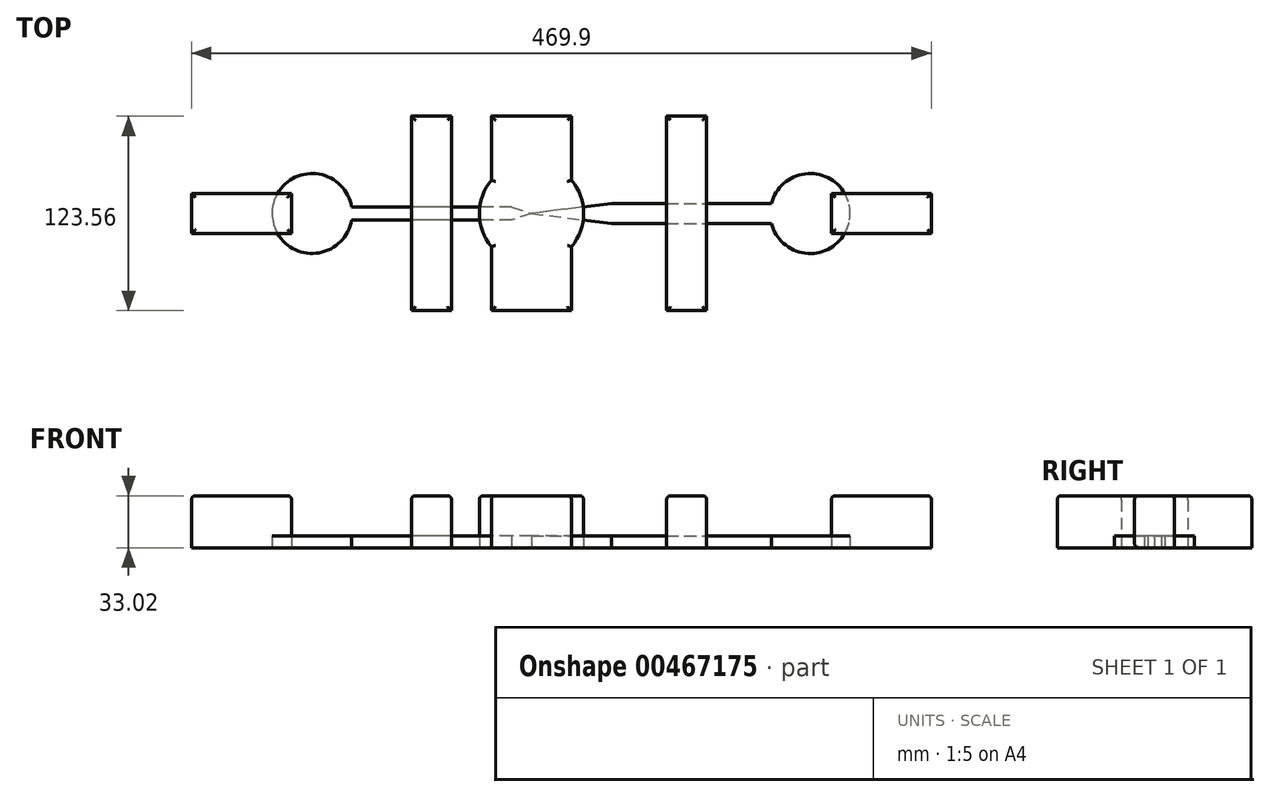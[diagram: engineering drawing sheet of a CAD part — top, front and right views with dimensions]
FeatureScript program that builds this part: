
annotation { "Feature Type Name" : "Feature", "Feature Type Description" : "" }
export const myFeature = defineFeature(function(context is Context, id is Id, definition is map)
    precondition{}
    {
        {
            var Q0;
            Q0=qCreatedBy(makeId("Top.planeOp"),FACE);
            var sketch = newSketch(context, id + "F0", { "sketchPlane" : qUnion([Q0])});
            skLineSegment(sketch, "E0.bottom", {"start": v(50.8, 4.22) * mm, "end": v(-50.8, 4.22) * mm});
            skLineSegment(sketch, "E0.top", {"start": v(50.8, -4.22) * mm, "end": v(-50.8, -4.22) * mm});
            skLineSegment(sketch, "E0.left", {"start": v(50.8, 4.22) * mm, "end": v(50.8, -4.22) * mm});
            skLineSegment(sketch, "E0.right", {"start": v(-50.8, 4.22) * mm, "end": v(-50.8, -4.22) * mm});
            skPoint(sketch, "E0.middle", {"position": v(0, 0) * mm});
            skLineSegment(sketch, "E1", {"start": v(50.8, 4.22) * mm, "end": v(63.5, 0) * mm});
            skLineSegment(sketch, "E2", {"start": v(63.5, 0) * mm, "end": v(50.8, -4.22) * mm});
            skCircle(sketch, "E3", {"center": v(-75.85, 0) * mm, "radius": 25.4 * mm});
            skPoint(sketch, "E3.third.point", {"position": v(-101.25, 0) * mm});
            skPoint(sketch, "E3.third.point.positionSnap0", {"position": v(-50.8, 0) * mm});
            skLineSegment(sketch, "E4.bottom", {"start": v(114.3, 6.45) * mm, "end": v(215.9, 6.45) * mm});
            skLineSegment(sketch, "E4.top", {"start": v(114.3, -6.45) * mm, "end": v(215.9, -6.45) * mm});
            skLineSegment(sketch, "E4.left", {"start": v(114.3, 6.45) * mm, "end": v(114.3, -6.45) * mm});
            skLineSegment(sketch, "E4.right", {"start": v(215.9, 6.45) * mm, "end": v(215.9, -6.45) * mm});
            skPoint(sketch, "E4.middle", {"position": v(165.1, 0) * mm});
            skLineSegment(sketch, "E5", {"start": v(114.3, 6.45) * mm, "end": v(63.5, 0) * mm});
            skLineSegment(sketch, "E6", {"start": v(63.5, 0) * mm, "end": v(114.3, -6.45) * mm});
            skCircle(sketch, "E7", {"center": v(240.47, 0) * mm, "radius": 25.4 * mm});
            skPoint(sketch, "E7.third.point", {"position": v(265.03, -6.45) * mm});
            skCircle(sketch, "E8", {"center": v(63.5, 0) * mm, "radius": 31.15 * mm});
            skLineSegment(sketch, "E9.bottom", {"start": v(-12.7, -76.2) * mm, "end": v(12.7, -76.2) * mm});
            skLineSegment(sketch, "E9.top", {"start": v(-12.7, 76.2) * mm, "end": v(12.7, 76.2) * mm});
            skLineSegment(sketch, "E9.left", {"start": v(-12.7, -76.2) * mm, "end": v(-12.7, 76.2) * mm});
            skLineSegment(sketch, "E9.right", {"start": v(12.7, -76.2) * mm, "end": v(12.7, 76.2) * mm});
            skLineSegment(sketch, "E10.bottom", {"start": v(152.4, 76.2) * mm, "end": v(177.8, 76.2) * mm});
            skLineSegment(sketch, "E10.top", {"start": v(152.4, -76.2) * mm, "end": v(177.8, -76.2) * mm});
            skLineSegment(sketch, "E10.left", {"start": v(152.4, 76.2) * mm, "end": v(152.4, -76.2) * mm});
            skLineSegment(sketch, "E10.right", {"start": v(177.8, 76.2) * mm, "end": v(177.8, -76.2) * mm});
            skLineSegment(sketch, "E11.bottom", {"start": v(12.7, 88.9) * mm, "end": v(342.9, 88.9) * mm, "construction": true});
            skLineSegment(sketch, "E11.top", {"start": v(12.7, 63.5) * mm, "end": v(342.9, 63.5) * mm, "construction": true});
            skLineSegment(sketch, "E11.left", {"start": v(12.7, 88.9) * mm, "end": v(12.7, 63.5) * mm, "construction": true});
            skLineSegment(sketch, "E11.right", {"start": v(342.9, 88.9) * mm, "end": v(342.9, 63.5) * mm, "construction": true});
            skPoint(sketch, "E11.middle", {"position": v(177.8, 76.2) * mm});
            skLineSegment(sketch, "E12.bottom", {"start": v(12.7, -88.9) * mm, "end": v(342.9, -88.9) * mm, "construction": true});
            skLineSegment(sketch, "E12.top", {"start": v(12.7, -63.5) * mm, "end": v(342.9, -63.5) * mm, "construction": true});
            skLineSegment(sketch, "E12.left", {"start": v(12.7, -88.9) * mm, "end": v(12.7, -63.5) * mm, "construction": true});
            skLineSegment(sketch, "E12.right", {"start": v(342.9, -88.9) * mm, "end": v(342.9, -63.5) * mm, "construction": true});
            skPoint(sketch, "E12.middle", {"position": v(177.8, -76.2) * mm});
            skLineSegment(sketch, "E13.bottom", {"start": v(40.98, 63.5) * mm, "end": v(86.02, 63.5) * mm});
            skLineSegment(sketch, "E13.top", {"start": v(40.98, -63.5) * mm, "end": v(86.02, -63.5) * mm});
            skLineSegment(sketch, "E13.left", {"start": v(40.98, 63.5) * mm, "end": v(40.98, -63.5) * mm});
            skLineSegment(sketch, "E13.right", {"start": v(86.02, 63.5) * mm, "end": v(86.02, -63.5) * mm});
            skSolve(sketch);
        }
        {
            var Q0;
            {var subQ0=sQuery(id+"F0.wireOp",EDGE,"E0.right");Q0=makeQuery(id+"F0.imprint","IMPRINT",FACE,{"disambiguationData":[TD([[makeQuery(id+"F0.imprint","IMPRINT",EDGE,{"derivedFrom":subQ0}),-1.0]])]});}
            var Q1;
            {var subQ0=sQuery(id+"F0.wireOp",EDGE,"E4.right");Q1=makeQuery(id+"F0.imprint","IMPRINT",FACE,{"disambiguationData":[TD([[makeQuery(id+"F0.imprint","IMPRINT",EDGE,{"derivedFrom":subQ0}),1.0]])]});}
            var Q2;
            {var subQ0=sQuery(id+"F0.wireOp",EDGE,"E8");var subQ1=sQuery(id+"F0.wireOp",EDGE,"E0.bottom");var subQ2=makeQuery(id+"F0.imprint","INTERSECT",VERTEX,{"derivedFrom":[subQ1,subQ0]});Q2=makeQuery(id+"F0.imprint","IMPRINT",FACE,{"disambiguationData":[TD([[makeQuery(id+"F0.imprint","IMPRINT",EDGE,{"disambiguationData":[TD([[subQ2,-1.0]])],"derivedFrom":subQ1}),1.0]])]});}
            var Q3;
            {var subQ2=sQuery(id+"F0.wireOp",EDGE,"E0.bottom");var subQ4=sQuery(id+"F0.wireOp",EDGE,"E9.left");var subQ5=makeQuery(id+"F0.imprint","INTERSECT",VERTEX,{"derivedFrom":[subQ2,subQ4]});Q3=makeQuery(id+"F0.imprint","IMPRINT",FACE,{"disambiguationData":[TD([[makeQuery(id+"F0.imprint","IMPRINT",EDGE,{"disambiguationData":[TD([[subQ5,1.0]])],"derivedFrom":subQ4}),1.0]])]});}
            var Q4;
            {var subQ0=sQuery(id+"F0.wireOp",EDGE,"E0.right");Q4=makeQuery(id+"F0.imprint","IMPRINT",FACE,{"disambiguationData":[TD([[makeQuery(id+"F0.imprint","IMPRINT",EDGE,{"derivedFrom":subQ0}),1.0]])]});}
            var Q5;
            {var subQ0=sQuery(id+"F0.wireOp",EDGE,"E4.left");Q5=makeQuery(id+"F0.imprint","IMPRINT",FACE,{"disambiguationData":[TD([[makeQuery(id+"F0.imprint","IMPRINT",EDGE,{"derivedFrom":subQ0}),1.0]])]});}
            var Q6;
            {var subQ2=sQuery(id+"F0.wireOp",EDGE,"E4.bottom");var subQ4=sQuery(id+"F0.wireOp",EDGE,"E10.right");var subQ5=makeQuery(id+"F0.imprint","INTERSECT",VERTEX,{"derivedFrom":[subQ2,subQ4]});Q6=makeQuery(id+"F0.imprint","IMPRINT",FACE,{"disambiguationData":[TD([[makeQuery(id+"F0.imprint","IMPRINT",EDGE,{"disambiguationData":[TD([[subQ5,-1.0]])],"derivedFrom":subQ4}),1.0]])]});}
            var Q7;
            {var subQ0=sQuery(id+"F0.wireOp",EDGE,"E4.left");Q7=makeQuery(id+"F0.imprint","IMPRINT",FACE,{"disambiguationData":[TD([[makeQuery(id+"F0.imprint","IMPRINT",EDGE,{"derivedFrom":subQ0}),-1.0]])]});}
            var Q8;
            {var subQ0=sQuery(id+"F0.wireOp",EDGE,"E4.right");Q8=makeQuery(id+"F0.imprint","IMPRINT",FACE,{"disambiguationData":[TD([[makeQuery(id+"F0.imprint","IMPRINT",EDGE,{"derivedFrom":subQ0}),-1.0]])]});}
            var Q9;
            {var subQ0=sQuery(id+"F0.wireOp",EDGE,"E8");var subQ1=sQuery(id+"F0.wireOp",EDGE,"E0.bottom");var subQ2=makeQuery(id+"F0.imprint","INTERSECT",VERTEX,{"derivedFrom":[subQ1,subQ0]});Q9=makeQuery(id+"F0.imprint","IMPRINT",FACE,{"disambiguationData":[TD([[makeQuery(id+"F0.imprint","IMPRINT",EDGE,{"disambiguationData":[TD([[subQ2,1.0]])],"derivedFrom":subQ1}),1.0]])]});}
            var Q10;
            {var subQ0=sQuery(id+"F0.wireOp",EDGE,"E8");var subQ1=sQuery(id+"F0.wireOp",EDGE,"E5");var subQ2=makeQuery(id+"F0.imprint","INTERSECT",VERTEX,{"derivedFrom":[subQ1,subQ0]});Q10=makeQuery(id+"F0.imprint","IMPRINT",FACE,{"disambiguationData":[TD([[makeQuery(id+"F0.imprint","IMPRINT",EDGE,{"disambiguationData":[TD([[subQ2,-1.0]])],"derivedFrom":subQ1}),1.0]])]});}
            var Q11;
            {var subQ0=sQuery(id+"F0.wireOp",EDGE,"E0.left");Q11=makeQuery(id+"F0.imprint","IMPRINT",FACE,{"disambiguationData":[TD([[makeQuery(id+"F0.imprint","IMPRINT",EDGE,{"derivedFrom":subQ0}),-1.0]])]});}
            var Q12;
            Q12=makeQuery(id+"F0.imprint","IMPRINT",FACE,{"disambiguationData":[TD([[makeQuery(id+"F0.imprint","IMPRINT",EDGE,{"derivedFrom":sQuery(id+"F0.wireOp",EDGE,"E0.left")}),1.0]])]});
            var Q13;
            {var subQ1=sQuery(id+"F0.wireOp",EDGE,"E5");var subQ3=sQuery(id+"F0.wireOp",EDGE,"E13.right");var subQ4=makeQuery(id+"F0.imprint","INTERSECT",VERTEX,{"derivedFrom":[subQ1,subQ3]});Q13=makeQuery(id+"F0.imprint","IMPRINT",FACE,{"disambiguationData":[TD([[makeQuery(id+"F0.imprint","IMPRINT",EDGE,{"disambiguationData":[TD([[subQ4,-1.0]])],"derivedFrom":subQ3}),-1.0]])]});}
            var Q14;
            {var subQ0=sQuery(id+"F0.wireOp",EDGE,"E10.left");var subQ1=sQuery(id+"F0.wireOp",EDGE,"E4.bottom");var subQ2=makeQuery(id+"F0.imprint","INTERSECT",VERTEX,{"derivedFrom":[subQ1,subQ0]});Q14=makeQuery(id+"F0.imprint","IMPRINT",FACE,{"disambiguationData":[TD([[makeQuery(id+"F0.imprint","IMPRINT",EDGE,{"disambiguationData":[TD([[subQ2,-1.0]])],"derivedFrom":subQ1}),-1.0]])]});}
            var Q15;
            {var subQ0=sQuery(id+"F0.wireOp",EDGE,"E9.right");var subQ1=sQuery(id+"F0.wireOp",EDGE,"E0.bottom");var subQ2=makeQuery(id+"F0.imprint","INTERSECT",VERTEX,{"derivedFrom":[subQ1,subQ0]});Q15=makeQuery(id+"F0.imprint","IMPRINT",FACE,{"disambiguationData":[TD([[makeQuery(id+"F0.imprint","IMPRINT",EDGE,{"disambiguationData":[TD([[subQ2,-1.0]])],"derivedFrom":subQ1}),1.0]])]});}
            extrude(context, id + "F1", {"entities" : qUnion([Q0, Q1, Q2, Q3, Q4, Q5, Q6, Q7, Q8, Q9, Q10, Q11, Q12, Q13, Q14, Q15]), "depth" : 7.62 * mm});
        }
        {
            var Q0;
            Q0=makeQuery(id+"F1.opExtrude","CAP_FACE",FACE,{"disambiguationData":[OSD([sQuery(id+"F0.wireOp",EDGE,"E0.bottom"),sQuery(id+"F0.wireOp",EDGE,"E0.top"),sQuery(id+"F0.wireOp",EDGE,"E1"),sQuery(id+"F0.wireOp",EDGE,"E2"),sQuery(id+"F0.wireOp",EDGE,"E3")])],"isStart":false});
            var sketch = newSketch(context, id + "F2", { "sketchPlane" : qUnion([Q0])});
            skCircle(sketch, "E14", {"center": v(63.5, 0) * mm, "radius": 33.09 * mm});
            skLineSegment(sketch, "E15.bottom", {"start": v(-12.7, 61.78) * mm, "end": v(12.7, 61.78) * mm});
            skLineSegment(sketch, "E15.top", {"start": v(-12.7, -61.78) * mm, "end": v(12.7, -61.78) * mm});
            skLineSegment(sketch, "E15.left", {"start": v(-12.7, 61.78) * mm, "end": v(-12.7, -61.78) * mm});
            skLineSegment(sketch, "E15.right", {"start": v(12.7, 61.78) * mm, "end": v(12.7, -61.78) * mm});
            skPoint(sketch, "E15.middle", {"position": v(0, 0) * mm});
            skLineSegment(sketch, "E16.bottom", {"start": v(149.36, 61.78) * mm, "end": v(174.76, 61.78) * mm});
            skLineSegment(sketch, "E16.top", {"start": v(149.36, -61.78) * mm, "end": v(174.76, -61.78) * mm});
            skLineSegment(sketch, "E16.left", {"start": v(149.36, 61.78) * mm, "end": v(149.36, -61.78) * mm});
            skLineSegment(sketch, "E16.right", {"start": v(174.76, 61.78) * mm, "end": v(174.76, -61.78) * mm});
            skPoint(sketch, "E16.middle", {"position": v(162.06, 0) * mm});
            skLineSegment(sketch, "E17.bottom", {"start": v(88.9, 61.78) * mm, "end": v(38.1, 61.78) * mm});
            skLineSegment(sketch, "E17.top", {"start": v(88.9, -61.78) * mm, "end": v(38.1, -61.78) * mm});
            skLineSegment(sketch, "E17.left", {"start": v(88.9, 61.78) * mm, "end": v(88.9, -61.78) * mm});
            skLineSegment(sketch, "E17.right", {"start": v(38.1, 61.78) * mm, "end": v(38.1, -61.78) * mm});
            skLineSegment(sketch, "E18.bottom", {"start": v(-88.9, 12.7) * mm, "end": v(-152.4, 12.7) * mm});
            skLineSegment(sketch, "E18.top", {"start": v(-88.9, -12.7) * mm, "end": v(-152.4, -12.7) * mm});
            skLineSegment(sketch, "E18.left", {"start": v(-88.9, 12.7) * mm, "end": v(-88.9, -12.7) * mm});
            skLineSegment(sketch, "E18.right", {"start": v(-152.4, 12.7) * mm, "end": v(-152.4, -12.7) * mm});
            skLineSegment(sketch, "E19.bottom", {"start": v(254, 12.7) * mm, "end": v(317.5, 12.7) * mm});
            skLineSegment(sketch, "E19.top", {"start": v(254, -12.7) * mm, "end": v(317.5, -12.7) * mm});
            skLineSegment(sketch, "E19.left", {"start": v(254, 12.7) * mm, "end": v(254, -12.7) * mm});
            skLineSegment(sketch, "E19.right", {"start": v(317.5, 12.7) * mm, "end": v(317.5, -12.7) * mm});
            skSolve(sketch);
        }
        {
            var Q0;
            Q0=makeQuery(id+"F2.imprint","IMPRINT",FACE,{"disambiguationData":[TD([[makeQuery(id+"F2.imprint","IMPRINT",EDGE,{"derivedFrom":sQuery(id+"F2.wireOp",EDGE,"E16.bottom")}),-1.0]])]});
            var Q1;
            Q1=makeQuery(id+"F2.imprint","IMPRINT",FACE,{"disambiguationData":[TD([[makeQuery(id+"F2.imprint","IMPRINT",EDGE,{"derivedFrom":sQuery(id+"F2.wireOp",EDGE,"E19.bottom")}),-1.0]])]});
            var Q2;
            {var subQ5=sQuery(id+"F2.wireOp",EDGE,"E17.bottom");Q2=makeQuery(id+"F2.imprint","IMPRINT",FACE,{"disambiguationData":[TD([[makeQuery(id+"F2.imprint","IMPRINT",EDGE,{"derivedFrom":subQ5}),1.0]])]});}
            var Q3;
            {var subQ5=sQuery(id+"F2.wireOp",EDGE,"E17.top");Q3=makeQuery(id+"F2.imprint","IMPRINT",FACE,{"disambiguationData":[TD([[makeQuery(id+"F2.imprint","IMPRINT",EDGE,{"derivedFrom":subQ5}),-1.0]])]});}
            var Q4;
            {var subQ0=sQuery(id+"F2.wireOp",EDGE,"E17.left");var subQ1=sQuery(id+"F2.wireOp",EDGE,"E14");var subQ2=makeQuery(id+"F2.imprint","INTERSECT",VERTEX,{"disambiguationData":[OD(0.0)],"derivedFrom":[subQ1,subQ0]});Q4=makeQuery(id+"F2.imprint","IMPRINT",FACE,{"disambiguationData":[TD([[makeQuery(id+"F2.imprint","IMPRINT",EDGE,{"disambiguationData":[TD([[subQ2,1.0]])],"derivedFrom":subQ1}),1.0]])]});}
            var Q5;
            {var subQ0=sQuery(id+"F2.wireOp",EDGE,"E15.bottom");Q5=makeQuery(id+"F2.imprint","IMPRINT",FACE,{"disambiguationData":[TD([[makeQuery(id+"F2.imprint","IMPRINT",EDGE,{"derivedFrom":subQ0}),-1.0]])]});}
            var Q6;
            {var subQ0=sQuery(id+"F2.wireOp",EDGE,"E15.top");Q6=makeQuery(id+"F2.imprint","IMPRINT",FACE,{"disambiguationData":[TD([[makeQuery(id+"F2.imprint","IMPRINT",EDGE,{"derivedFrom":subQ0}),1.0]])]});}
            var Q7;
            {var subQ0=sQuery(id+"F2.wireOp",EDGE,"E17.right");var subQ1=sQuery(id+"F2.wireOp",EDGE,"E14");var subQ2=makeQuery(id+"F2.imprint","INTERSECT",VERTEX,{"disambiguationData":[OD(0.0)],"derivedFrom":[subQ1,subQ0]});Q7=makeQuery(id+"F2.imprint","IMPRINT",FACE,{"disambiguationData":[TD([[makeQuery(id+"F2.imprint","IMPRINT",EDGE,{"disambiguationData":[TD([[subQ2,-1.0]])],"derivedFrom":subQ1}),1.0]])]});}
            var Q8;
            {var subQ0=sQuery(id+"F2.wireOp",EDGE,"E17.right");var subQ1=sQuery(id+"F2.wireOp",EDGE,"E14");var subQ2=makeQuery(id+"F2.imprint","INTERSECT",VERTEX,{"disambiguationData":[OD(1.0)],"derivedFrom":[subQ1,subQ0]});Q8=makeQuery(id+"F2.imprint","IMPRINT",FACE,{"disambiguationData":[TD([[makeQuery(id+"F2.imprint","IMPRINT",EDGE,{"disambiguationData":[TD([[subQ2,1.0]])],"derivedFrom":subQ1}),1.0]])]});}
            var Q9;
            {var subQ0=sQuery(id+"F2.wireOp",EDGE,"E18.left");Q9=makeQuery(id+"F2.imprint","IMPRINT",FACE,{"disambiguationData":[TD([[makeQuery(id+"F2.imprint","IMPRINT",EDGE,{"derivedFrom":subQ0}),-1.0]])]});}
            var Q10;
            {var subQ0=makeQuery(id+"F1.opExtrude","CAP_EDGE",EDGE,{"disambiguationData":[OSD([sQuery(id+"F0.wireOp",EDGE,"E1")])],"isStart":false});Q10=makeQuery(id+"F2.imprint","IMPRINT",FACE,{"disambiguationData":[TD([[makeQuery(id+"F2.imprint","IMPRINT",EDGE,{"derivedFrom":subQ0}),-1.0]])]});}
            var Q11;
            {var subQ0=sQuery(id+"F2.wireOp",EDGE,"E14");var subQ1=makeQuery(id+"F1.opExtrude","CAP_EDGE",EDGE,{"disambiguationData":[OSD([sQuery(id+"F0.wireOp",EDGE,"E0.bottom")])],"isStart":false});var subQ2=makeQuery(id+"F2.imprint","INTERSECT",VERTEX,{"derivedFrom":[subQ1,subQ0]});Q11=makeQuery(id+"F2.imprint","IMPRINT",FACE,{"disambiguationData":[TD([[makeQuery(id+"F2.imprint","IMPRINT",EDGE,{"disambiguationData":[TD([[subQ2,-1.0]])],"derivedFrom":subQ0}),1.0]])]});}
            var Q12;
            {var subQ0=sQuery(id+"F2.wireOp",EDGE,"E15.left");var subQ1=makeQuery(id+"F1.opExtrude","CAP_EDGE",EDGE,{"disambiguationData":[OSD([sQuery(id+"F0.wireOp",EDGE,"E0.bottom")])],"isStart":false});var subQ2=makeQuery(id+"F2.imprint","INTERSECT",VERTEX,{"derivedFrom":[subQ1,subQ0]});Q12=makeQuery(id+"F2.imprint","IMPRINT",FACE,{"disambiguationData":[TD([[makeQuery(id+"F2.imprint","IMPRINT",EDGE,{"disambiguationData":[TD([[subQ2,-1.0]])],"derivedFrom":subQ0}),1.0]])]});}
            var Q13;
            {var subQ12=makeQuery(id+"F1.opExtrude","CAP_EDGE",EDGE,{"disambiguationData":[OSD([sQuery(id+"F0.wireOp",EDGE,"E1")])],"isStart":false});Q13=makeQuery(id+"F2.imprint","IMPRINT",FACE,{"disambiguationData":[TD([[makeQuery(id+"F2.imprint","IMPRINT",EDGE,{"derivedFrom":subQ12}),1.0]])]});}
            var Q14;
            {var subQ0=sQuery(id+"F2.wireOp",EDGE,"E18.right");Q14=makeQuery(id+"F2.imprint","IMPRINT",FACE,{"disambiguationData":[TD([[makeQuery(id+"F2.imprint","IMPRINT",EDGE,{"derivedFrom":subQ0}),1.0]])]});}
            extrude(context, id + "F3", {"entities" : qUnion([Q0, Q1, Q2, Q3, Q4, Q5, Q6, Q7, Q8, Q9, Q10, Q11, Q12, Q13, Q14]), "depth" : 25.4 * mm, "hasSecondDirection" : true, "secondDirectionOppositeDirection" : true, "secondDirectionDepth" : 7.62 * mm});
        }
        {
            var Q0;
            Q0=makeQuery(id+"F3.opExtrude","CAP_EDGE",EDGE,{"disambiguationData":[OSD([sQuery(id+"F2.wireOp",EDGE,"E19.top")])],"isStart":true});
            var Q1;
            Q1=makeQuery(id+"F3.opExtrude","CAP_FACE",FACE,{"disambiguationData":[OSD([sQuery(id+"F2.wireOp",EDGE,"E19.bottom"),sQuery(id+"F2.wireOp",EDGE,"E19.top"),sQuery(id+"F2.wireOp",EDGE,"E19.left"),sQuery(id+"F2.wireOp",EDGE,"E19.right")])],"isStart":false});
            var Q2;
            Q2=makeQuery(id+"F3.opExtrude","CAP_FACE",FACE,{"disambiguationData":[OSD([sQuery(id+"F2.wireOp",EDGE,"E16.bottom"),sQuery(id+"F2.wireOp",EDGE,"E16.top"),sQuery(id+"F2.wireOp",EDGE,"E16.left"),sQuery(id+"F2.wireOp",EDGE,"E16.right")])],"isStart":false});
            var Q3;
            Q3=makeQuery(id+"F3.opExtrude","CAP_FACE",FACE,{"disambiguationData":[OSD([sQuery(id+"F2.wireOp",EDGE,"E14"),sQuery(id+"F2.wireOp",EDGE,"E17.bottom"),sQuery(id+"F2.wireOp",EDGE,"E17.top"),sQuery(id+"F2.wireOp",EDGE,"E17.left"),sQuery(id+"F2.wireOp",EDGE,"E17.right")])],"isStart":false});
            var Q4;
            Q4=makeQuery(id+"F3.opExtrude","CAP_FACE",FACE,{"disambiguationData":[OSD([sQuery(id+"F2.wireOp",EDGE,"E15.bottom"),sQuery(id+"F2.wireOp",EDGE,"E15.top"),sQuery(id+"F2.wireOp",EDGE,"E15.left"),sQuery(id+"F2.wireOp",EDGE,"E15.right")])],"isStart":false});
            var Q5;
            Q5=makeQuery(id+"F3.opExtrude","CAP_FACE",FACE,{"disambiguationData":[OSD([sQuery(id+"F2.wireOp",EDGE,"E18.bottom"),sQuery(id+"F2.wireOp",EDGE,"E18.top"),sQuery(id+"F2.wireOp",EDGE,"E18.left"),sQuery(id+"F2.wireOp",EDGE,"E18.right")])],"isStart":false});
            fillet(context, id + "F4", {"entities" : qUnion([Q0, Q1, Q2, Q3, Q4, Q5]), "radius" : 2.54 * mm, "tangentPropagation" : true, "allowEdgeOverflow" : false});
        }
    });
